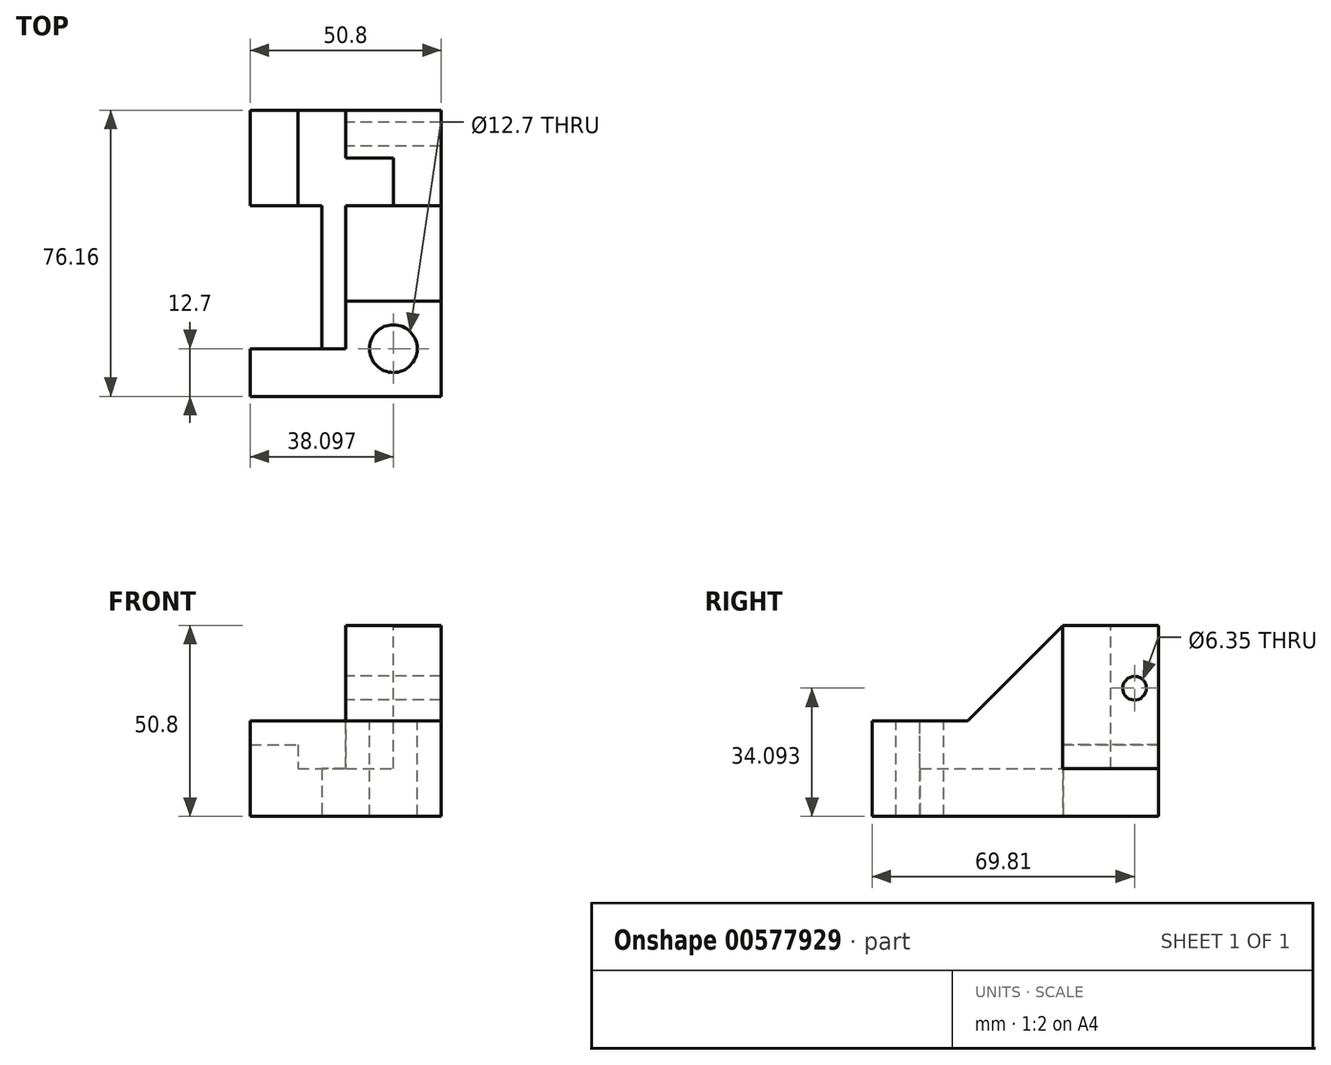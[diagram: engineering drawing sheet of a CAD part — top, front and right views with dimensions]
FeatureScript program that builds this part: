
annotation { "Feature Type Name" : "Feature", "Feature Type Description" : "" }
export const myFeature = defineFeature(function(context is Context, id is Id, definition is map)
    precondition{}
    {
        {
            var Q0;
            Q0=qCreatedBy(makeId("Front.planeOp"),FACE);
            var sketch = newSketch(context, id + "F0", { "sketchPlane" : qUnion([Q0])});
            skLineSegment(sketch, "E0", {"start": v(-26.15, -45.91) * mm, "end": v(24.65, -45.91) * mm});
            skLineSegment(sketch, "E1", {"start": v(24.65, -45.91) * mm, "end": v(24.65, -20.51) * mm});
            skLineSegment(sketch, "E2", {"start": v(24.65, -20.51) * mm, "end": v(-26.15, -20.51) * mm});
            skLineSegment(sketch, "E3", {"start": v(-26.15, -20.51) * mm, "end": v(-26.15, -45.91) * mm});
            skSolve(sketch);
        }
        {
            var Q0;
            Q0 = qSketchRegion(id + "F0", true);
            extrude(context, id + "F1", {"entities" : qUnion([Q0]), "depth" : 25.4 * mm, "offsetDistance" : 25.4 * mm});
        }
        {
            var Q0;
            Q0=makeQuery(id+"F1.opExtrude","SWEPT_FACE",FACE,{"disambiguationData":[OSD([sQuery(id+"F0.wireOp",EDGE,"E2")])]});
            var sketch = newSketch(context, id + "F2", { "sketchPlane" : qUnion([Q0])});
            skLineSegment(sketch, "E4", {"start": v(-26.15, -12.7) * mm, "end": v(-0.75, -12.7) * mm});
            skLineSegment(sketch, "E5", {"start": v(-0.75, -12.7) * mm, "end": v(-0.75, 0) * mm});
            skLineSegment(sketch, "E6", {"start": v(24.65, -25.4) * mm, "end": v(11.95, -25.4) * mm, "construction": true});
            skLineSegment(sketch, "E7", {"start": v(11.95, -25.4) * mm, "end": v(11.95, -12.7) * mm, "construction": true});
            skCircle(sketch, "E8", {"center": v(11.95, -12.7) * mm, "radius": 6.35 * mm});
            skSolve(sketch);
        }
        {
            var Q0;
            {var subQ0=sQuery(id+"F2.wireOp",EDGE,"E4");Q0=makeQuery(id+"F2.imprint","IMPRINT",FACE,{"disambiguationData":[TD([[makeQuery(id+"F2.imprint","IMPRINT",EDGE,{"derivedFrom":subQ0}),1.0]])]});}
            var Q1;
            Q1=makeQuery(id+"F2.imprint","IMPRINT",FACE,{"disambiguationData":[TD([[makeQuery(id+"F2.imprint","IMPRINT",EDGE,{"derivedFrom":sQuery(id+"F2.wireOp",EDGE,"E8")}),1.0]])]});
            extrude(context, id + "F3", {"entities" : qUnion([Q0, Q1]), "operationType" : NewBodyOperationType.REMOVE, "endBound" : BoundingType.THROUGH_ALL, "oppositeDirection" : true, "depth" : 25.4 * mm, "offsetDistance" : 25.4 * mm});
        }
        {
            var Q0;
            Q0=makeQuery(id+"F3.boolean.opBoolean","COPY",FACE,{"derivedFrom":makeQuery(id+"F3.opExtrude","SWEPT_FACE",FACE,{"disambiguationData":[OSD([sQuery(id+"F2.wireOp",EDGE,"E5")])]})});
            cPlane(context, id + "F4", {"entities" : qUnion([Q0]), "cplaneType" : CPlaneType.OFFSET, "offset" : 0 * mm, "width" : 152.4 * mm, "height" : 152.4 * mm});
        }
        {
            var Q0;
            Q0=qCreatedBy(id+"F4.planeOp",FACE);
            var sketch = newSketch(context, id + "F5", { "sketchPlane" : qUnion([Q0])});
            skLineSegment(sketch, "E9", {"start": v(-25.4, 4.86) * mm, "end": v(-25.4, -33.24) * mm});
            skLineSegment(sketch, "E10", {"start": v(-25.4, -33.24) * mm, "end": v(12.7, -33.24) * mm});
            skLineSegment(sketch, "E11", {"start": v(-25.4, 4.86) * mm, "end": v(0, -20.54) * mm});
            skLineSegment(sketch, "E12", {"start": v(0, -20.54) * mm, "end": v(12.7, -33.24) * mm});
            skSolve(sketch);
        }
        {
            var Q0;
            Q0 = qSketchRegion(id + "F5", true);
            extrude(context, id + "F6", {"entities" : qUnion([Q0]), "operationType" : NewBodyOperationType.ADD, "oppositeDirection" : true, "depth" : 25.4 * mm, "offsetDistance" : 25.4 * mm});
        }
        {
            var Q0;
            Q0=makeQuery(id+"F1.opExtrude","SWEPT_FACE",FACE,{"disambiguationData":[OSD([sQuery(id+"F0.wireOp",EDGE,"E2")])]});
            cPlane(context, id + "F7", {"entities" : qUnion([Q0]), "cplaneType" : CPlaneType.OFFSET, "offset" : 25.4 * mm, "width" : 152.4 * mm, "height" : 152.4 * mm});
        }
        {
            var Q0;
            Q0=qCreatedBy(id+"F7.planeOp",FACE);
            var sketch = newSketch(context, id + "F8", { "sketchPlane" : qUnion([Q0])});
            skLineSegment(sketch, "E13", {"start": v(-0.75, 38.08) * mm, "end": v(-0.75, 50.76) * mm});
            skLineSegment(sketch, "E14", {"start": v(-0.75, 50.76) * mm, "end": v(24.65, 50.76) * mm});
            skLineSegment(sketch, "E15", {"start": v(-0.75, 38.08) * mm, "end": v(11.95, 38.08) * mm});
            skLineSegment(sketch, "E16", {"start": v(11.95, 38.08) * mm, "end": v(11.95, 25.34) * mm});
            skLineSegment(sketch, "E17", {"start": v(24.65, 50.76) * mm, "end": v(24.65, 25.34) * mm});
            skLineSegment(sketch, "E18", {"start": v(11.95, 25.34) * mm, "end": v(24.65, 25.34) * mm});
            skSolve(sketch);
        }
        {
            var Q0;
            Q0 = qSketchRegion(id + "F8", true);
            extrude(context, id + "F9", {"entities" : qUnion([Q0]), "operationType" : NewBodyOperationType.ADD, "oppositeDirection" : true, "depth" : 38.1 * mm, "offsetDistance" : 25.4 * mm});
        }
        {
            var Q0;
            Q0=makeQuery(id+"F1.opExtrude","SWEPT_FACE",FACE,{"disambiguationData":[OSD([sQuery(id+"F0.wireOp",EDGE,"E2")])]});
            cPlane(context, id + "F10", {"entities" : qUnion([Q0]), "cplaneType" : CPlaneType.OFFSET, "offset" : 25.4 * mm, "oppositeDirection" : true, "width" : 152.4 * mm, "height" : 152.4 * mm});
        }
        {
            var Q0;
            Q0=qCreatedBy(id+"F10.planeOp",FACE);
            var sketch = newSketch(context, id + "F11", { "sketchPlane" : qUnion([Q0])});
            skLineSegment(sketch, "E19", {"start": v(-0.75, 50.76) * mm, "end": v(-26.15, 50.76) * mm});
            skLineSegment(sketch, "E20", {"start": v(-7.1, -12.7) * mm, "end": v(-7.1, 25.4) * mm});
            skLineSegment(sketch, "E21", {"start": v(-26.15, 25.34) * mm, "end": v(-7.1, 25.4) * mm});
            skLineSegment(sketch, "E22", {"start": v(-0.75, 50.76) * mm, "end": v(24.65, 50.76) * mm});
            skLineSegment(sketch, "E23", {"start": v(24.65, 50.76) * mm, "end": v(24.65, 0) * mm});
            skLineSegment(sketch, "E24", {"start": v(24.65, 0) * mm, "end": v(-0.75, 0) * mm});
            skLineSegment(sketch, "E25", {"start": v(-0.75, 0) * mm, "end": v(-0.75, -12.7) * mm});
            skLineSegment(sketch, "E26", {"start": v(-0.75, -12.7) * mm, "end": v(-7.1, -12.7) * mm});
            skLineSegment(sketch, "E27", {"start": v(-26.15, 25.34) * mm, "end": v(-26.15, 50.76) * mm});
            skSolve(sketch);
        }
        {
            var Q0;
            Q0 = qSketchRegion(id + "F11", true);
            extrude(context, id + "F12", {"entities" : qUnion([Q0]), "operationType" : NewBodyOperationType.ADD, "depth" : 12.7 * mm, "offsetDistance" : 25.4 * mm});
        }
        {
            var Q0;
            Q0=makeQuery(id+"F12.opExtrude","CAP_FACE",FACE,{"disambiguationData":[OSD([sQuery(id+"F11.wireOp",EDGE,"E19"),sQuery(id+"F11.wireOp",EDGE,"KBAEWt1v-VUL3-O8Bz-9CWo-QaUx3Arg21dP"),sQuery(id+"F11.wireOp",EDGE,"E20"),sQuery(id+"F11.wireOp",EDGE,"E21"),sQuery(id+"F11.wireOp",EDGE,"E22"),sQuery(id+"F11.wireOp",EDGE,"E23"),sQuery(id+"F11.wireOp",EDGE,"E24"),sQuery(id+"F11.wireOp",EDGE,"E25"),sQuery(id+"F11.wireOp",EDGE,"E26")])],"isStart":false});
            var sketch = newSketch(context, id + "F13", { "sketchPlane" : qUnion([Q0])});
            skLineSegment(sketch, "E28", {"start": v(-13.45, 50.76) * mm, "end": v(-13.45, 25.38) * mm});
            skLineSegment(sketch, "E29", {"start": v(-13.45, 25.38) * mm, "end": v(-26.15, 25.34) * mm});
            skLineSegment(sketch, "E30", {"start": v(-26.15, 25.34) * mm, "end": v(-26.15, 50.76) * mm});
            skLineSegment(sketch, "E31", {"start": v(-26.15, 50.76) * mm, "end": v(-13.45, 50.76) * mm});
            skSolve(sketch);
        }
        {
            var Q0;
            Q0=makeQuery(id+"F13.imprint","IMPRINT",FACE,{"disambiguationData":[TD([[makeQuery(id+"F13.imprint","IMPRINT",EDGE,{"derivedFrom":sQuery(id+"F13.wireOp",EDGE,"E28")}),-1.0]])]});
            extrude(context, id + "F14", {"entities" : qUnion([Q0]), "operationType" : NewBodyOperationType.ADD, "depth" : 6.35 * mm, "offsetDistance" : 25.4 * mm});
        }
        {
            var Q0;
            Q0=makeQuery(id+"F9.opExtrude","SWEPT_FACE",FACE,{"disambiguationData":[OSD([sQuery(id+"F8.wireOp",EDGE,"E13")])]});
            var sketch = newSketch(context, id + "F15", { "sketchPlane" : qUnion([Q0])});
            skLineSegment(sketch, "E32", {"start": v(-50.76, -30.87) * mm, "end": v(-50.76, -11.82) * mm, "construction": true});
            skLineSegment(sketch, "E33", {"start": v(-50.76, -11.82) * mm, "end": v(-44.4, -11.82) * mm, "construction": true});
            skCircle(sketch, "E34", {"center": v(-44.4, -11.82) * mm, "radius": 3.18 * mm});
            skSolve(sketch);
        }
        {
            var Q0;
            Q0=makeQuery(id+"F15.imprint","IMPRINT",FACE,{"disambiguationData":[TD([[makeQuery(id+"F15.imprint","IMPRINT",EDGE,{"derivedFrom":sQuery(id+"F15.wireOp",EDGE,"E34")}),1.0]])]});
            extrude(context, id + "F16", {"entities" : qUnion([Q0]), "operationType" : NewBodyOperationType.REMOVE, "endBound" : BoundingType.THROUGH_ALL, "oppositeDirection" : true, "depth" : 25.4 * mm, "offsetDistance" : 25.4 * mm});
        }
        {
            var Q0;
            Q0=makeQuery(id+"F6.boolean.opBoolean","SPLIT",FACE,{"disambiguationData":[TD([makeQuery(id+"F3.boolean.opBoolean","COPY",FACE,{"derivedFrom":makeQuery(id+"F3.opExtrude","SWEPT_FACE",FACE,{"disambiguationData":[OSD([sQuery(id+"F2.wireOp",EDGE,"E8")])]})})])],"derivedFrom":makeQuery(id+"F6.opExtrude","SWEPT_FACE",FACE,{"disambiguationData":[OSD([sQuery(id+"F5.wireOp",EDGE,"E10")])]})});
            extrude(context, id + "F17", {"entities" : qUnion([Q0]), "operationType" : NewBodyOperationType.REMOVE, "endBound" : BoundingType.THROUGH_ALL, "oppositeDirection" : true, "depth" : 25.4 * mm, "offsetDistance" : 25.4 * mm});
        }
    });
